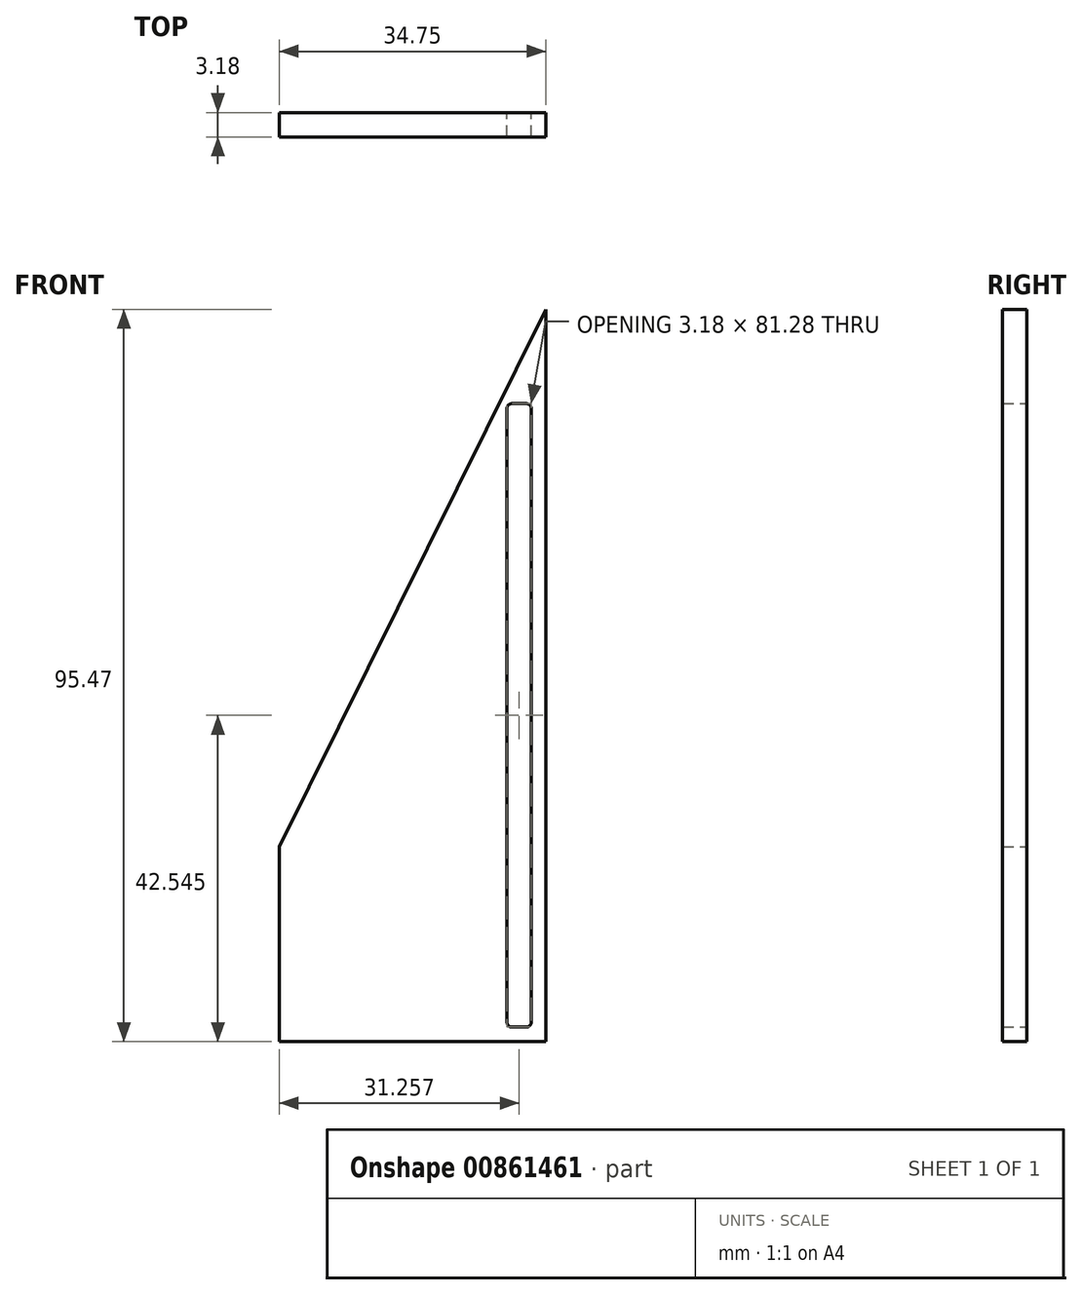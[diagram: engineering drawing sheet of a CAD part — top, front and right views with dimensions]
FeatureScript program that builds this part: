
annotation { "Feature Type Name" : "Feature", "Feature Type Description" : "" }
export const myFeature = defineFeature(function(context is Context, id is Id, definition is map)
    precondition{}
    {
        {
            var Q0;
            Q0=qCreatedBy(makeId("Front.planeOp"),FACE);
            var sketch = newSketch(context, id + "F0", { "sketchPlane" : qUnion([Q0])});
            skLineSegment(sketch, "E0", {"start": v(0, 0) * mm, "end": v(34.75, 0) * mm});
            skLineSegment(sketch, "E1", {"start": v(34.75, 0) * mm, "end": v(34.75, 95.47) * mm});
            skLineSegment(sketch, "E2", {"start": v(0, 0) * mm, "end": v(0, 25.4) * mm});
            skLineSegment(sketch, "E3", {"start": v(0, 25.4) * mm, "end": v(34.75, 95.47) * mm});
            skLineSegment(sketch, "E4.bottom", {"start": v(30.3, 1.9) * mm, "end": v(32.2, 1.9) * mm});
            skLineSegment(sketch, "E4.top", {"start": v(30.3, 83.19) * mm, "end": v(32.2, 83.19) * mm});
            skLineSegment(sketch, "E4.left", {"start": v(29.67, 2.54) * mm, "end": v(29.67, 82.55) * mm});
            skLineSegment(sketch, "E4.right", {"start": v(32.84, 2.54) * mm, "end": v(32.84, 82.55) * mm});
            skPoint(sketch, "E5.visualSharp", {"position": v(32.84, 83.19) * mm});
            skArc(sketch, "E5.filletArc", {"start": v(32.84, 82.55) * mm, "mid": v(32.66, 83) * mm, "end": v(32.2, 83.19) * mm});
            skPoint(sketch, "E6.visualSharp", {"position": v(29.67, 83.19) * mm});
            skArc(sketch, "E6.filletArc", {"start": v(30.3, 83.19) * mm, "mid": v(29.86, 83) * mm, "end": v(29.67, 82.55) * mm});
            skPoint(sketch, "E7.visualSharp", {"position": v(32.84, 1.9) * mm});
            skArc(sketch, "E7.filletArc", {"start": v(32.2, 1.9) * mm, "mid": v(32.66, 2.1) * mm, "end": v(32.84, 2.54) * mm});
            skPoint(sketch, "E8.visualSharp", {"position": v(29.67, 1.9) * mm});
            skArc(sketch, "E8.filletArc", {"start": v(29.67, 2.54) * mm, "mid": v(29.86, 2.1) * mm, "end": v(30.3, 1.9) * mm});
            skSolve(sketch);
        }
        {
            var Q0;
            Q0 = qSketchRegion(id + "F0", true);
            extrude(context, id + "F1", {"entities" : qUnion([Q0]), "depth" : 3.17 * mm, "offsetDistance" : 25.4 * mm, "symmetric" : true});
        }
    });
